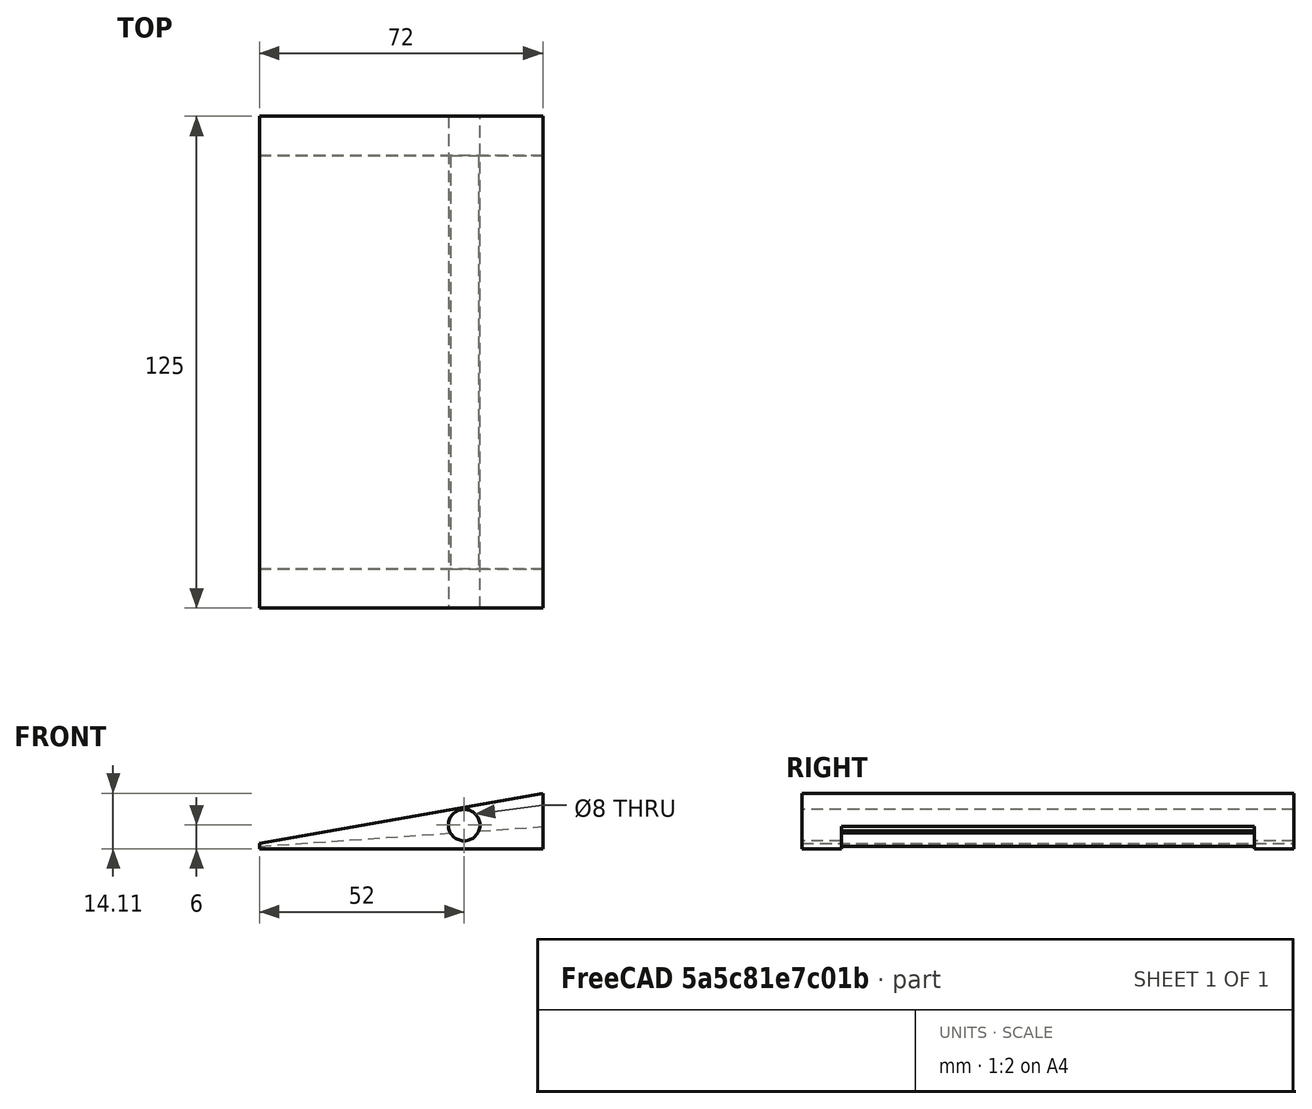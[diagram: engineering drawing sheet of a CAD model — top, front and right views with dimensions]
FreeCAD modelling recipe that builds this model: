
FCSTD DOCUMENT  (FreeCAD 1.0R38642 (Git))
Label: Belt_sander_angle_guide2
License: All rights reserved
LicenseURL: https://en.wikipedia.org/wiki/All_rights_reserved
objects: Part::Box×4, Part::Cut×4, Spreadsheet::Sheet×1, Part::Cylinder×1, App::Part×1
note: 9 computed .brp shape members not serialized (recipe doc carries the construction recipe); baked Part::Feature solids carry a one-line shape summary decoded from their .brp

FEATURE [Spreadsheet::Sheet] Spreadsheet
  cells = A1='belt mouth width; B1(belt_mouth_width)=105; A2='frame width; B2(frame_width)=125; A3='grind angle; B3(grind_angle)=10; A4='guide length; B4(guide_length)=80
FEATURE [Part::Box] Box  label="base_frame"
  AttacherType = Attacher::AttachEngine3D
  Height = 50
  Length = 80
  Width = 125
  expr: Length = Spreadsheet.guide_length
  expr: Width = Spreadsheet.frame_width
FEATURE [Part::Box] Box001  label="belt_cutout"
  AttacherType = Attacher::AttachEngine3D
  Height = 13
  Length = 85
  Placement = pos=(0,10,-13) rot=(0,1,0;-0.069813rad)
  Width = 105
  expr: .Placement.Base.y = (Spreadsheet.frame_width - Spreadsheet.belt_mouth_width) / 2
  expr: Length = Spreadsheet.guide_length + 5
  expr: Width = Spreadsheet.belt_mouth_width
FEATURE [Part::Box] Box002  label="guide_cutout"
  AttacherType = Attacher::AttachEngine3D
  Height = 50
  Length = 90
  Placement = pos=(0,0,0) rot=(0,-1,0;0.174533rad)
  Width = 125
  expr: .Placement.Rotation.Angle = Spreadsheet.grind_angle
  expr: Length = Spreadsheet.guide_length + 10
  expr: Width = Spreadsheet.frame_width
FEATURE [Part::Cut] Cut
  Base = -> Box
  Tool = -> Box001
FEATURE [Part::Cut] Cut001
  Base = -> Cut
  Tool = -> Box002
FEATURE [Part::Box] Box003  label="edge_remove"
  AttacherType = Attacher::AttachEngine3D
  Height = 2
  Length = 8
  Width = 125
  expr: Width = Spreadsheet.frame_width
FEATURE [Part::Cut] Cut002
  Base = -> Cut001
  Tool = -> Box003
FEATURE [Part::Cylinder] Cylinder  label="mount_hole"
  Angle = 360
  AttacherType = Attacher::AttachEngine3D
  FirstAngle = 0
  Height = 125
  Placement = pos=(60,0,6) rot=(-1,0,0;1.5708rad)
  Radius = 4
  SecondAngle = 0
  expr: Height = Spreadsheet.frame_width
FEATURE [Part::Cut] Cut003
  Base = -> Cut002
  Tool = -> Cylinder
FEATURE [App::Part] Part
  Group = -> [Cut,Box001,Box,Box003,Box002,Cut001,Cut002,Cylinder,Cut003]
  Origin = -> Origin
